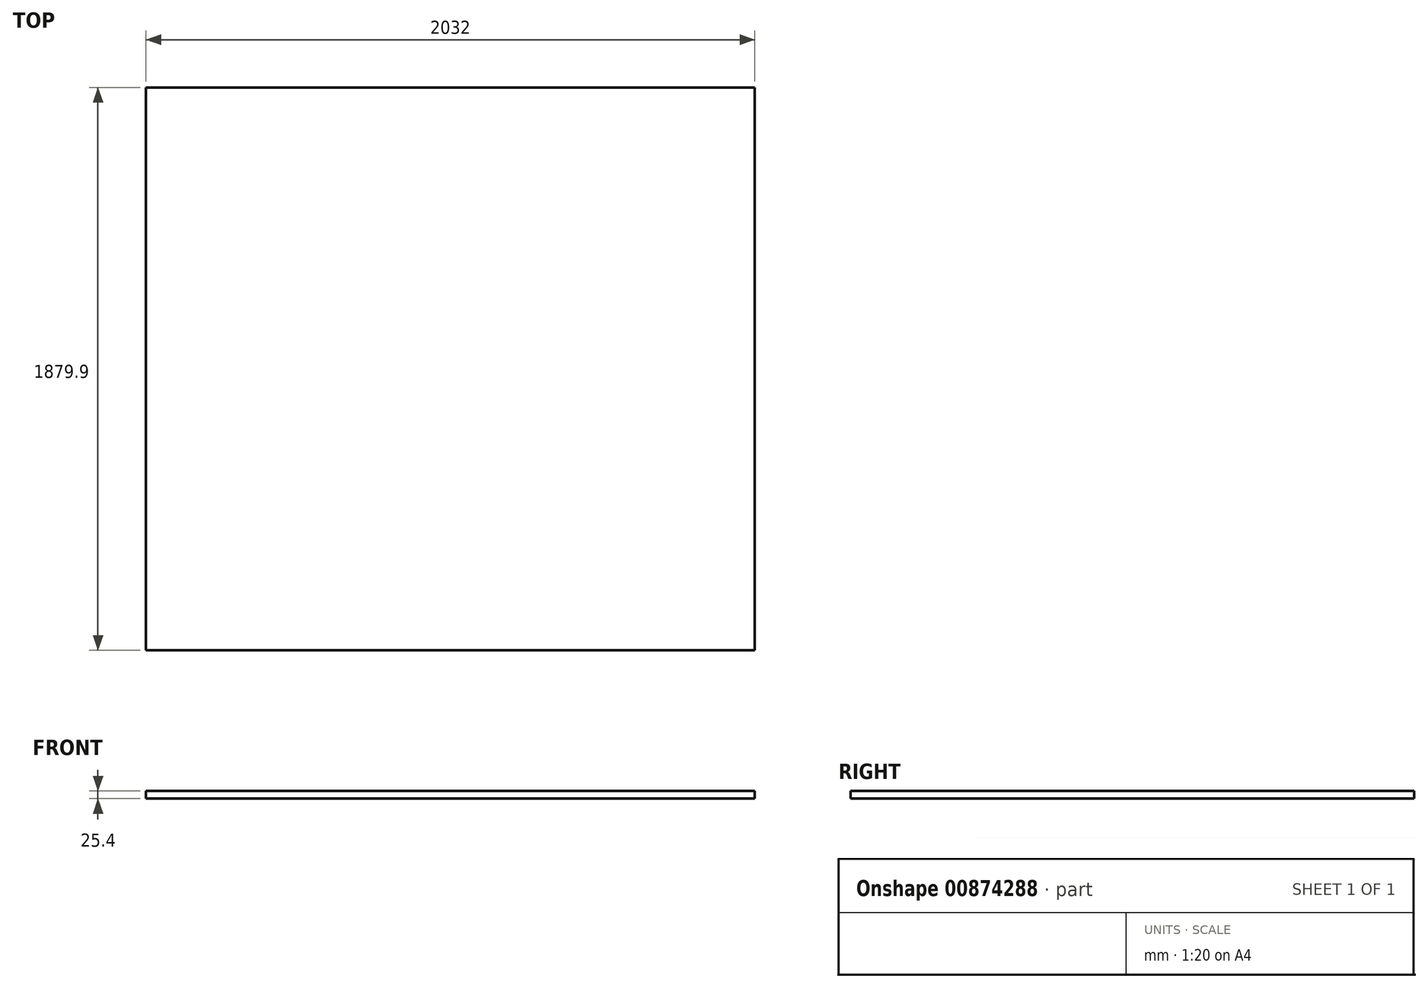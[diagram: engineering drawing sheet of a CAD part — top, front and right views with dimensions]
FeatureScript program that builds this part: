
annotation { "Feature Type Name" : "Feature", "Feature Type Description" : "" }
export const myFeature = defineFeature(function(context is Context, id is Id, definition is map)
    precondition{}
    {
        {
            var Q0;
            Q0=qCreatedBy(makeId("Top.planeOp"),FACE);
            var sketch = newSketch(context, id + "F0", { "sketchPlane" : qUnion([Q0])});
            skLineSegment(sketch, "E0.bottom", {"start": v(-1014.32, 936.01) * mm, "end": v(1017.68, 936.01) * mm});
            skLineSegment(sketch, "E0.top", {"start": v(-1014.32, -943.9) * mm, "end": v(1017.68, -943.9) * mm});
            skLineSegment(sketch, "E0.left", {"start": v(-1014.32, 936.01) * mm, "end": v(-1014.32, -943.9) * mm});
            skLineSegment(sketch, "E0.right", {"start": v(1017.68, 936.01) * mm, "end": v(1017.68, -943.9) * mm});
            skSolve(sketch);
        }
        {
            var Q0;
            Q0=makeQuery(id+"F0.imprint","IMPRINT",FACE,{"disambiguationData":[TD([[makeQuery(id+"F0.imprint","IMPRINT",EDGE,{"derivedFrom":sQuery(id+"F0.wireOp",EDGE,"E0.bottom")}),-1.0]])]});
            extrude(context, id + "F1", {"entities" : qUnion([Q0]), "depth" : 25.4 * mm, "offsetDistance" : 25.4 * mm});
        }
    });
